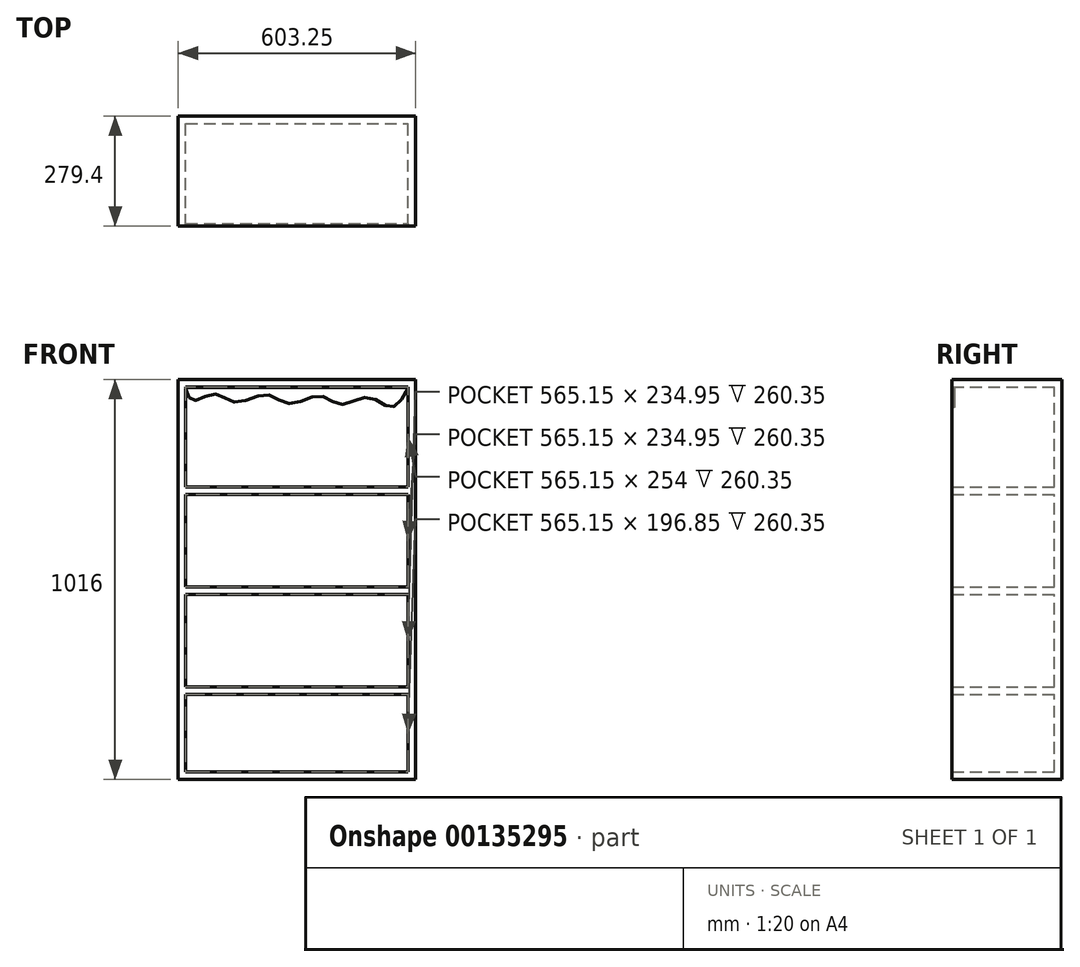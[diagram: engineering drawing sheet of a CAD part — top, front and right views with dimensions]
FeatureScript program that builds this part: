
annotation { "Feature Type Name" : "Feature", "Feature Type Description" : "" }
export const myFeature = defineFeature(function(context is Context, id is Id, definition is map)
    precondition{}
    {
        {
            var Q0;
            Q0=qCreatedBy(makeId("Front.planeOp"),FACE);
            var sketch = newSketch(context, id + "F0", { "sketchPlane" : qUnion([Q0])});
            skLineSegment(sketch, "E0.bottom", {"start": v(0, 0) * mm, "end": v(603.25, 0) * mm});
            skLineSegment(sketch, "E0.top", {"start": v(0, 1016) * mm, "end": v(603.25, 1016) * mm});
            skLineSegment(sketch, "E0.left", {"start": v(0, 0) * mm, "end": v(0, 1016) * mm});
            skLineSegment(sketch, "E0.right", {"start": v(603.25, 0) * mm, "end": v(603.25, 1016) * mm});
            skSolve(sketch);
        }
        {
            var Q0;
            Q0 = qSketchRegion(id + "F0", true);
            extrude(context, id + "F1", {"entities" : qUnion([Q0]), "depth" : 279.4 * mm});
        }
        {
            var Q0;
            Q0=makeQuery(id+"F1.opExtrude","CAP_FACE",FACE,{"disambiguationData":[OSD([sQuery(id+"F0.wireOp",EDGE,"E0.bottom"),sQuery(id+"F0.wireOp",EDGE,"E0.top"),sQuery(id+"F0.wireOp",EDGE,"E0.left"),sQuery(id+"F0.wireOp",EDGE,"E0.right")])],"isStart":false});
            shell(context, id + "F2", {"entities" : qUnion([Q0]), "thickness" : 19.05 * mm});
        }
        {
            var Q0;
            Q0=makeQuery(id+"F2.opShell","OFFSET_FACE",FACE,{"disambiguationData":[OSD([sQuery(id+"F0.wireOp",EDGE,"E0.bottom"),sQuery(id+"F0.wireOp",EDGE,"E0.top"),sQuery(id+"F0.wireOp",EDGE,"E0.left"),sQuery(id+"F0.wireOp",EDGE,"E0.right")])]});
            var sketch = newSketch(context, id + "F3", { "sketchPlane" : qUnion([Q0])});
            skLineSegment(sketch, "E1.bottom", {"start": v(19.05, 742.95) * mm, "end": v(584.2, 742.95) * mm});
            skLineSegment(sketch, "E1.top", {"start": v(19.05, 723.9) * mm, "end": v(584.2, 723.9) * mm});
            skLineSegment(sketch, "E1.left", {"start": v(19.05, 742.95) * mm, "end": v(19.05, 723.9) * mm});
            skLineSegment(sketch, "E1.right", {"start": v(584.2, 742.95) * mm, "end": v(584.2, 723.9) * mm});
            skLineSegment(sketch, "E2.0.1.0", {"start": v(19.05, 488.95) * mm, "end": v(584.2, 488.95) * mm});
            skLineSegment(sketch, "E2.0.1.1", {"start": v(19.05, 469.9) * mm, "end": v(584.2, 469.9) * mm});
            skLineSegment(sketch, "E2.0.1.2", {"start": v(19.05, 488.95) * mm, "end": v(19.05, 469.9) * mm});
            skLineSegment(sketch, "E2.0.1.3", {"start": v(584.2, 488.95) * mm, "end": v(584.2, 469.9) * mm});
            skLineSegment(sketch, "E2.0.2.0", {"start": v(19.05, 234.95) * mm, "end": v(584.2, 234.95) * mm});
            skLineSegment(sketch, "E2.0.2.1", {"start": v(19.05, 215.9) * mm, "end": v(584.2, 215.9) * mm});
            skLineSegment(sketch, "E2.0.2.2", {"start": v(19.05, 234.95) * mm, "end": v(19.05, 215.9) * mm});
            skLineSegment(sketch, "E2.0.2.3", {"start": v(584.2, 234.95) * mm, "end": v(584.2, 215.9) * mm});
            skLineSegment(sketch, "E2.direction1", {"start": v(19.05, 723.9) * mm, "end": v(30.97, 723.9) * mm, "construction": true});
            skLineSegment(sketch, "E2.direction2", {"start": v(19.05, 723.9) * mm, "end": v(19.05, 469.9) * mm, "construction": true});
            skSolve(sketch);
        }
        {
            var Q0;
            Q0 = qSketchRegion(id + "F3", true);
            extrude(context, id + "F4", {"entities" : qUnion([Q0]), "operationType" : NewBodyOperationType.ADD, "depth" : 260.35 * mm});
        }
        {
            var Q0;
            Q0=qCreatedBy(makeId("Front.planeOp"),FACE);
            cPlane(context, id + "F5", {"entities" : qUnion([Q0]), "cplaneType" : CPlaneType.OFFSET, "offset" : 279.4 * mm, "width" : 152.4 * mm, "height" : 152.4 * mm});
        }
        {
            var Q0;
            Q0=qCreatedBy(id+"F5.planeOp",FACE);
            var sketch = newSketch(context, id + "F6", { "sketchPlane" : qUnion([Q0])});
            skFitSpline(sketch, "E3", {"points": [v(18.38, 995.7) * mm, v(38.45, 962.85) * mm, v(93.2, 979.27) * mm, v(145.2, 958.29) * mm, v(223.65, 977.45) * mm, v(282.95, 954.64) * mm, v(356.85, 974.7) * mm, v(414.32, 952.81) * mm, v(483.66, 971.06) * mm, v(541.13, 945.52) * mm, v(584.92, 995.7) * mm], "startDerivative": vector(175.02, -598.67) * mm, "endDerivative": vector(392.6, 729.97) * mm});
            skLineSegment(sketch, "E4", {"start": v(18.38, 995.7) * mm, "end": v(584.92, 995.7) * mm});
            skSolve(sketch);
        }
        {
            var Q0;
            Q0 = qSketchRegion(id + "F6", true);
            extrude(context, id + "F7", {"entities" : qUnion([Q0]), "operationType" : NewBodyOperationType.ADD, "oppositeDirection" : true, "depth" : 6.35 * mm});
        }
    });
